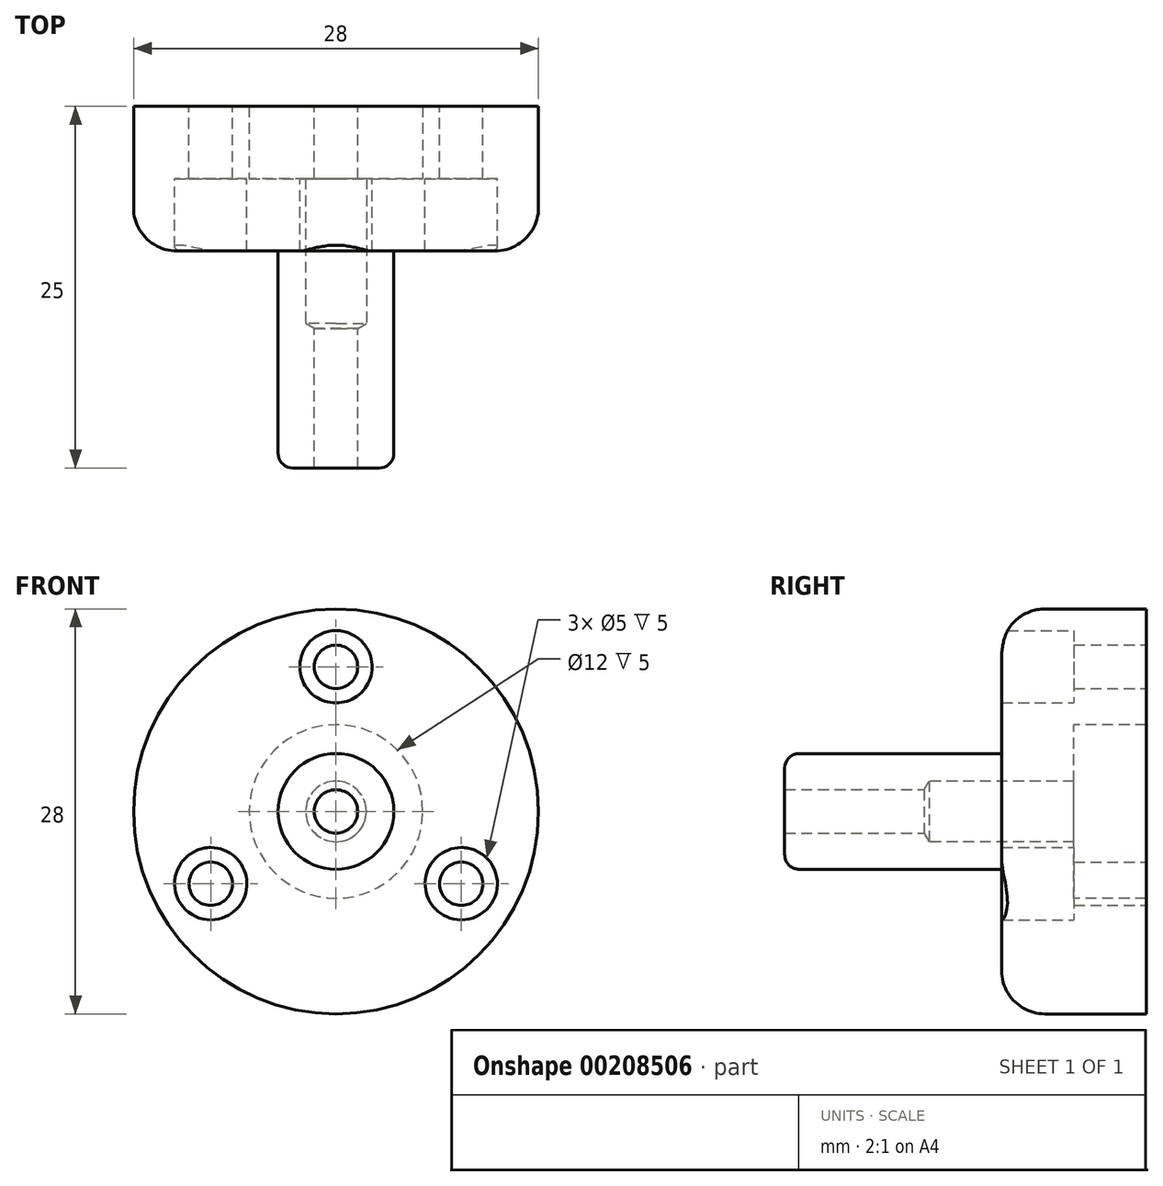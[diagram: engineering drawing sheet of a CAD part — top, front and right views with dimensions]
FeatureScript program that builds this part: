
annotation { "Feature Type Name" : "Feature", "Feature Type Description" : "" }
export const myFeature = defineFeature(function(context is Context, id is Id, definition is map)
    precondition{}
    {
        {
            var Q0;
            Q0=qCreatedBy(makeId("Front.planeOp"),FACE);
            var sketch = newSketch(context, id + "F0", { "sketchPlane" : qUnion([Q0])});
            skCircle(sketch, "E0", {"center": v(0, 0) * mm, "radius": 14 * mm});
            skSolve(sketch);
        }
        {
            var Q0;
            Q0 = qSketchRegion(id + "F0", true);
            extrude(context, id + "F1", {"entities" : qUnion([Q0]), "depth" : 10 * mm});
        }
        {
            var Q0;
            Q0=qCreatedBy(makeId("Front.planeOp"),FACE);
            var sketch = newSketch(context, id + "F2", { "sketchPlane" : qUnion([Q0])});
            skCircle(sketch, "E1", {"center": v(0, 0) * mm, "radius": 4 * mm});
            skSolve(sketch);
        }
        {
            var Q0;
            Q0 = qSketchRegion(id + "F2", true);
            extrude(context, id + "F3", {"entities" : qUnion([Q0]), "operationType" : NewBodyOperationType.ADD, "depth" : 25 * mm});
        }
        {
            var Q0;
            Q0=makeQuery(id+"F3.opExtrude","CAP_EDGE",EDGE,{"disambiguationData":[OSD([sQuery(id+"F2.wireOp",EDGE,"E1")])],"isStart":false});
            fillet(context, id + "F4", {"entities" : qUnion([Q0]), "radius" : 1 * mm, "tangentPropagation" : true, "allowEdgeOverflow" : false});
        }
        {
            var Q0;
            Q0=makeQuery(id+"F1.opExtrude","CAP_EDGE",EDGE,{"disambiguationData":[OSD([sQuery(id+"F0.wireOp",EDGE,"E0")])],"isStart":false});
            fillet(context, id + "F5", {"entities" : qUnion([Q0]), "radius" : 3 * mm, "tangentPropagation" : true, "allowEdgeOverflow" : false});
        }
        {
            var Q0;
            Q0=makeQuery(id+"F3.opExtrude","CAP_FACE",FACE,{"disambiguationData":[OSD([sQuery(id+"F2.wireOp",EDGE,"E1")])],"isStart":false});
            var sketch = newSketch(context, id + "F6", { "sketchPlane" : qUnion([Q0])});
            skCircle(sketch, "E2", {"center": v(0, 0) * mm, "radius": 1.5 * mm});
            skSolve(sketch);
        }
        {
            var Q0;
            Q0=sQuery(id+"F6.wireOp",VERTEX,"E2.center");
            var Q1;
            Q1=makeQuery(id+"F1.opExtrude","SWEPT_BODY",BODY,{"disambiguationData":[OSD([sQuery(id+"F0.wireOp",EDGE,"E0")])]});
            hole(context, id + "F7", {"style" : HoleStyle.SIMPLE, "endStyle" : HoleEndStyle.BLIND, "holeDiameter" : 3 * mm, "majorDiameter" : 5 * mm, "holeDepth" : 10 * mm, "locations" : qUnion([Q0]), "scope" : qUnion([Q1]), "tapClearance" : 3, "tappedDepth" : 12 * mm, "startStyle" : HoleStartStyle.SKETCH});
        }
        {
            var Q0;
            Q0=makeQuery(id+"F1.opExtrude","CAP_FACE",FACE,{"disambiguationData":[OSD([sQuery(id+"F0.wireOp",EDGE,"E0")])],"isStart":true});
            var sketch = newSketch(context, id + "F8", { "sketchPlane" : qUnion([Q0])});
            skCircle(sketch, "E3", {"center": v(0, 0) * mm, "radius": 2.5 * mm});
            skSolve(sketch);
        }
        {
            var Q0;
            Q0=sQuery(id+"F8.wireOp",VERTEX,"E3.center");
            var Q1;
            Q1=makeQuery(id+"F1.opExtrude","SWEPT_BODY",BODY,{"disambiguationData":[OSD([sQuery(id+"F0.wireOp",EDGE,"E0")])]});
            hole(context, id + "F9", {"style" : HoleStyle.C_BORE, "endStyle" : HoleEndStyle.BLIND, "holeDiameter" : 4.2 * mm, "cBoreDiameter" : 12 * mm, "cBoreDepth" : 5 * mm, "majorDiameter" : 5 * mm, "holeDepth" : 15 * mm, "locations" : qUnion([Q0]), "scope" : qUnion([Q1]), "tapClearance" : 3, "tappedDepth" : 12 * mm, "startStyle" : HoleStartStyle.SKETCH});
        }
        {
            var Q0;
            Q0=makeQuery(id+"F1.opExtrude","CAP_FACE",FACE,{"disambiguationData":[OSD([sQuery(id+"F0.wireOp",EDGE,"E0")])],"isStart":false});
            var sketch = newSketch(context, id + "F10", { "sketchPlane" : qUnion([Q0])});
            skCircle(sketch, "E4", {"center": v(0, 0) * mm, "radius": 10 * mm, "construction": true});
            skLineSegment(sketch, "E5.0", {"start": v(0, 10) * mm, "end": v(8.66, -5) * mm, "construction": true});
            skLineSegment(sketch, "E5.1", {"start": v(8.66, -5) * mm, "end": v(-8.66, -5) * mm, "construction": true});
            skLineSegment(sketch, "E5.2", {"start": v(-8.66, -5) * mm, "end": v(0, 10) * mm, "construction": true});
            skSolve(sketch);
        }
        {
            var Q0;
            Q0=sQuery(id+"F10.wireOp",VERTEX,"E5.0.start");
            var Q1;
            Q1=sQuery(id+"F10.wireOp",VERTEX,"E5.1.start");
            var Q2;
            Q2=sQuery(id+"F10.wireOp",VERTEX,"E5.2.start");
            var Q3;
            Q3=makeQuery(id+"F1.opExtrude","SWEPT_BODY",BODY,{"disambiguationData":[OSD([sQuery(id+"F0.wireOp",EDGE,"E0")])]});
            hole(context, id + "F11", {"style" : HoleStyle.C_BORE, "endStyle" : HoleEndStyle.THROUGH, "holeDiameter" : 3 * mm, "cBoreDiameter" : 5 * mm, "cBoreDepth" : 5 * mm, "locations" : qUnion([Q0, Q1, Q2]), "scope" : qUnion([Q3]), "isTappedThrough" : true, "startStyle" : HoleStartStyle.SKETCH});
        }
    });
